# Revit family: NBS_Senator_MeetingPods_Enclave4Windmill
name_source: partatom
category: Furniture
revit_build: Autodesk Revit 2018 (Build: 20190510_1515(x64)
units: mm (PartAtom-declared; Revit-internal decimal feet)

## family parameters
Always vertical = Yes
Cut with Voids When Loaded = No
Room Calculation Point = No
Shared = No
Work Plane-Based = No

## types (2) — shared parameters
Accessories = Monitor arms, PU desk accessories, desk top accessories, CPU holders, electrical accessories, coat hanger, name plate, A2 dry wipe board with hanger, A3 dry wipe board with hanger
AssetType = Fixed
Category = Pr_40_50_12_53:Meeting pods
DurationUnit = year
ExpectedLife = 10
FabricFinishOptions = Plymouth, fairfield, latymer, lancaster, silcoates, silverdale, st andrews, trevelyan, ulster, wellington, wesley, manchester,
Features = Internal frame with multi-layered acoustic foam, levelling adjusters, blazer fabric, outer vertical panels
Finish = Outer vertical panels upholstered in camira, blazer fabric Two tone is standard
FinishOptions = Carini walnut, mocha, autumn, strata oak, maple, highland oak, beech, winter oak, hacienda white, white, light grey, denim, clay, lemon sorbet
FrameMaterial = NBS_Senator_Aluminium_Rigid_Siver
FramesColour = Black, white
IfcExportAs = IfcFurnitureType
IfcExportType = USERDEFINED
InnerPanelMaterial1 = NBS_Senator_VirginWool_Lancaster
InnerPanelMaterial2 = NBS_Senator_VirginWool_Montcrest
IsBuiltIn = No
ManufacturerName = The Senator Group
ManufacturerURL = www.senator.co.uk
Material = Fabric, metal, plastic
NBSCertification = www.nationalbimlibrary.com/cert/wdwktxqi
NBSDescription = Meeting pods
NBSReference = 45-35-20/342
NominalDepth = 1950 mm
NominalHeight = 1400 mm  [stored 4.59318 ft]
NominalLength = 2950 mm  [stored 9.67848 ft]
NominalWidth = 2950 mm  [stored 9.67848 ft]
ProductInformation = http://www.thesenatorgroup.com
Status = UNSET
Style = Pods
SustainabilityPerformance = 99% recyclable
TableTopMaterial = NBS_Senator_Wood_HighlandOak_2
Uniclass2015Code = Pr_40_50_12_53
Uniclass2015Title = Meeting Pods
Uniclass2015Version = Products v1.16
Version = 1
WarrantyDescription = Senator warrants that its manufactured products are free from manufacturing defects - in materials or workmanship - for a period of ten (10) years on Senator Seating ranges; and fifteen (15) years on Senator Desking ranges - exceptions are listed below. Senator will repair or replace (at Senator’s sole discretion) with comparable free of charge materials / components, any product / component, which fails under normal use in a single shift environment, as a result of a defect in the materials and / or workmanship
WarrantyDurationParts = 10
WarrantyDurationUnit = year
WindmillDepth = 2950 mm  [stored 9.67848 ft]
WindmillWidth = 2950 mm  [stored 9.67848 ft]

## per-type parameters (varying)
| type | BIMObjectName | Description | ModelReference | Name | Size | WindmillHeight |
| PDEN4W14 | NBS_Senator_MeetingPods_Enclave4Windmill_PDEN4W14 | Enclave Windmill - 1400mm high | Pods-Enclave4Windmill_PDEN4W14 | MeetingPods_Enclave4Windmill_PDEN4W14_Senator | 1950 x 2950 x 1400 mm | 1400 mm  [stored 4.59318 ft] |
| PDEN4W18 | NBS_Senator_MeetingPods_Enclave4Windmill_PDEN4W18 | Enclave Windmill - 1800mm high | Pods-Enclave4Windmill_PDEN4W18 | MeetingPods_Enclave4Windmill_PDEN4W18_Senator | 1950 x 2950 x 1800 mm | 1800 mm  [stored 5.90551 ft] |

note: column(s) folded — value = type name in every type: ModelNumber

note: [stored X ft] marks values corroborated as IEEE doubles in the binary element streams (Revit-internal decimal feet)

## geometry (parser evidence)
native form markers: Sweep x5
no freeform markers — native parametric forms only
